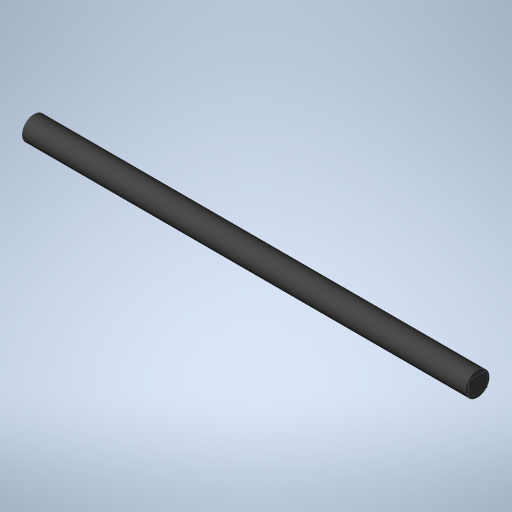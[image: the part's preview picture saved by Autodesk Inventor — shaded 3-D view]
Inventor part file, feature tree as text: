
AUTODESK INVENTOR PART (.ipt)
format: ipt  version: 2024.3 (Build 283343000, 343)  size: 246,272 bytes
history: native  units: mm
features: extrude x2, sketch x2
ambient origin geometry x8: Origin, YZ Plane, XZ Plane, XY Plane, X Axis, Y Axis, Z Axis, Center Point
bodies: Solid1 (feature_tree)
feature tree (4):
  extrude  "Extrusion1"  Depth=94.0mm TaperAngle=0.0deg
  extrude  "Extrusion2"  [1 undecoded]
  sketch  "Sketch1"  dims[d0=5.0mm d1=94.0mm d2=0.0mm]
  sketch  "Sketch2"  dims[d3=0.1mm d4=0.0mm]
note: 1 required parameter value undecoded (feature->parameter linkage not recoverable at this tier; creation-order binding heuristic only, values carry confidence <= 0.55)
